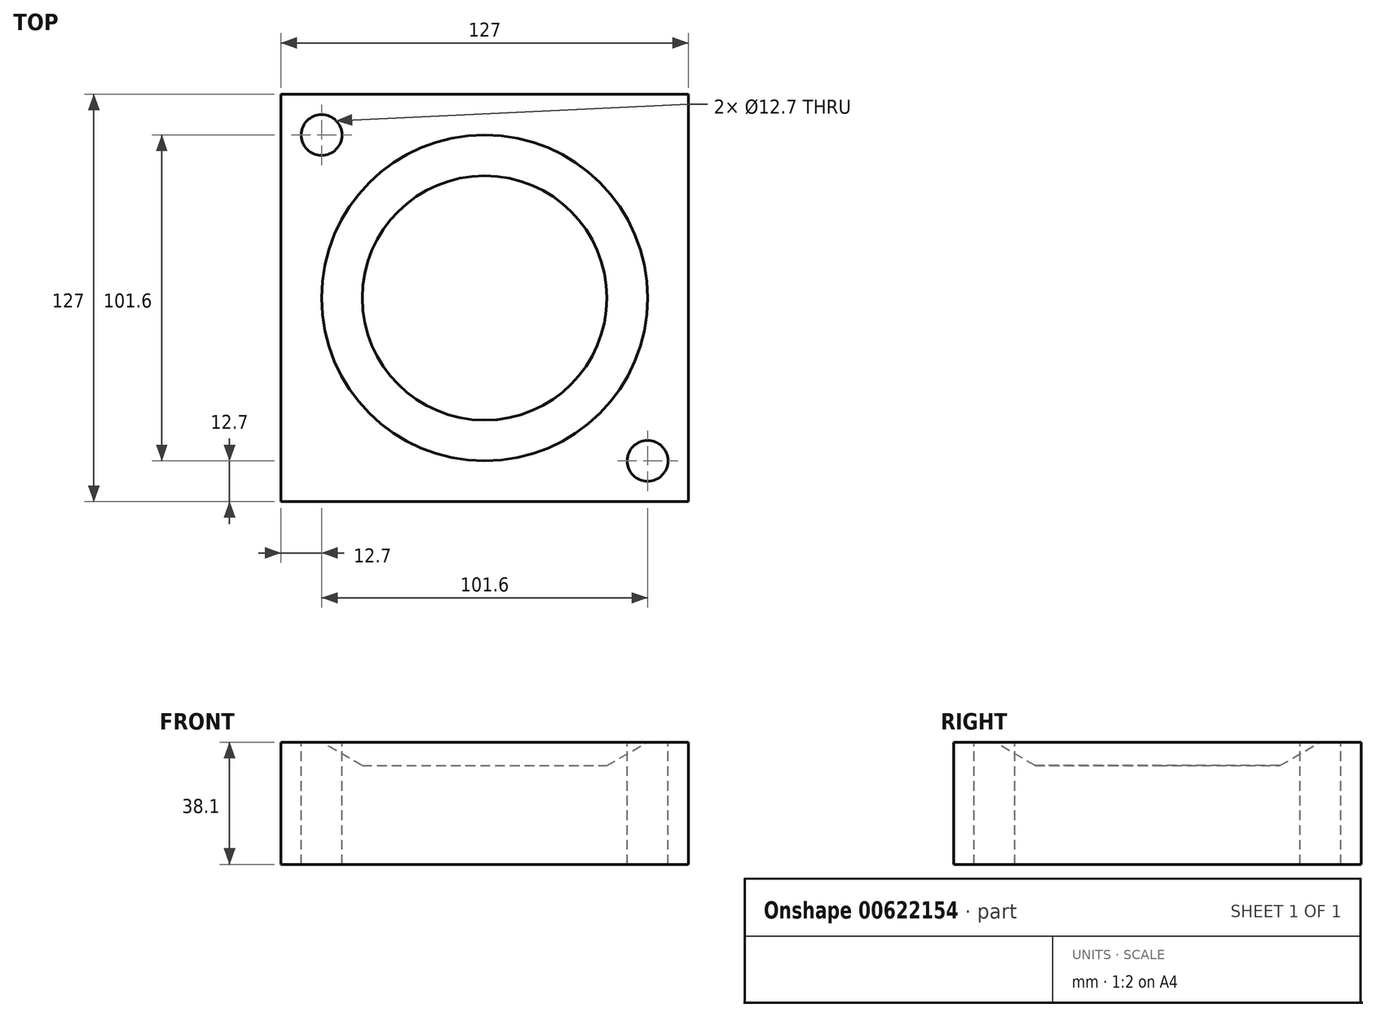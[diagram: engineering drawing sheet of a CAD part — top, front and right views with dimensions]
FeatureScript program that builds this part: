
annotation { "Feature Type Name" : "Feature", "Feature Type Description" : "" }
export const myFeature = defineFeature(function(context is Context, id is Id, definition is map)
    precondition{}
    {
        {
            var Q0;
            Q0=qCreatedBy(makeId("Front.planeOp"),FACE);
            var sketch = newSketch(context, id + "F0", { "sketchPlane" : qUnion([Q0])});
            skLineSegment(sketch, "E0", {"start": v(50.8, 5.8) * mm, "end": v(38.1, -1.52) * mm});
            skLineSegment(sketch, "E1", {"start": v(38.1, -1.52) * mm, "end": v(0, -1.52) * mm});
            skLineSegment(sketch, "E2", {"start": v(50.8, 5.8) * mm, "end": v(0, 5.8) * mm});
            skLineSegment(sketch, "E3", {"start": v(0, 5.8) * mm, "end": v(0, -1.52) * mm});
            skSolve(sketch);
        }
        {
            var Q0;
            Q0=qCreatedBy(makeId("Front.planeOp"),FACE);
            var sketch = newSketch(context, id + "F1", { "sketchPlane" : qUnion([Q0])});
            skLineSegment(sketch, "E4.top", {"start": v(63.5, -32.3) * mm, "end": v(-63.5, -32.3) * mm});
            skLineSegment(sketch, "E4.left", {"start": v(63.5, 5.8) * mm, "end": v(63.5, -32.3) * mm});
            skLineSegment(sketch, "E4.right", {"start": v(-63.5, 5.8) * mm, "end": v(-63.5, -32.3) * mm});
            skLineSegment(sketch, "E5", {"start": v(-63.5, 5.8) * mm, "end": v(0, 5.8) * mm});
            skLineSegment(sketch, "E6", {"start": v(0, 5.8) * mm, "end": v(63.5, 5.8) * mm});
            skSolve(sketch);
        }
        {
            var Q0;
            Q0 = qSketchRegion(id + "F1", true);
            extrude(context, id + "F2", {"entities" : qUnion([Q0]), "endBound" : BoundingType.SYMMETRIC, "depth" : 127 * mm, "offsetDistance" : 25.4 * mm});
        }
        {
            var Q0;
            Q0 = qSketchRegion(id + "F0", true);
            var Q1;
            Q1=sQuery(id+"F0.wireOp",EDGE,"E3");
            revolve(context, id + "F3", {"operationType" : NewBodyOperationType.REMOVE, "entities" : qUnion([Q0]), "axis" : qUnion([Q1]), "revolveType" : RevolveType.FULL, "oppositeDirection" : true});
        }
        {
            var Q0;
            Q0=qCreatedBy(makeId("Top.planeOp"),FACE);
            var sketch = newSketch(context, id + "F4", { "sketchPlane" : qUnion([Q0])});
            skLineSegment(sketch, "E7", {"start": v(-50.8, 0) * mm, "end": v(-50.8, 50.8) * mm});
            skLineSegment(sketch, "E8", {"start": v(-50.8, 50.8) * mm, "end": v(0, 50.8) * mm});
            skCircle(sketch, "E9", {"center": v(-50.8, 50.8) * mm, "radius": 6.35 * mm});
            skSolve(sketch);
        }
        {
            var Q0;
            Q0 = qSketchRegion(id + "F4", true);
            extrude(context, id + "F5", {"entities" : qUnion([Q0]), "operationType" : NewBodyOperationType.REMOVE, "endBound" : BoundingType.SYMMETRIC, "oppositeDirection" : true, "depth" : 101.6 * mm, "offsetDistance" : 25.4 * mm});
        }
        {
            var Q0;
            Q0=qCreatedBy(makeId("Top.planeOp"),FACE);
            var sketch = newSketch(context, id + "F6", { "sketchPlane" : qUnion([Q0])});
            skLineSegment(sketch, "E10", {"start": v(0, -50.8) * mm, "end": v(50.8, -50.8) * mm});
            skLineSegment(sketch, "E11", {"start": v(50.8, -50.8) * mm, "end": v(50.8, 0) * mm});
            skCircle(sketch, "E12", {"center": v(50.8, -50.8) * mm, "radius": 6.35 * mm});
            skSolve(sketch);
        }
        {
            var Q0;
            Q0 = qSketchRegion(id + "F6", true);
            extrude(context, id + "F7", {"entities" : qUnion([Q0]), "operationType" : NewBodyOperationType.REMOVE, "endBound" : BoundingType.SYMMETRIC, "oppositeDirection" : true, "depth" : 101.6 * mm, "offsetDistance" : 25.4 * mm});
        }
    });
